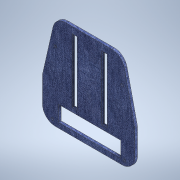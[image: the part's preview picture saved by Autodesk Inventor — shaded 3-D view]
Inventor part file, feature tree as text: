
AUTODESK INVENTOR PART (.ipt)
format: ipt  version: 2020 (Build 240168000, 168)  size: 148,992 bytes
history: native  units: in
note: dims shown in document units (in); Inventor stores cm internally (conversion verified against a paired STEP export)
features: extrude x1, fillet x1, sketch x1
ambient origin geometry x8: Origin, YZ Plane, XZ Plane, XY Plane, X Axis, Y Axis, Z Axis, Center Point
bodies: Solid1 (feature_tree)
feature tree (3):
  extrude  "Extrusion1"  Depth=0.9843in
  fillet  "Fillet1"  [1 undecoded]
  sketch  "Sketch1"  dims[d6=0.1969in d7=0.0in d8=0.9843in]
note: 1 required parameter value undecoded (feature->parameter linkage not recoverable at this tier; creation-order binding heuristic only, values carry confidence <= 0.55)
